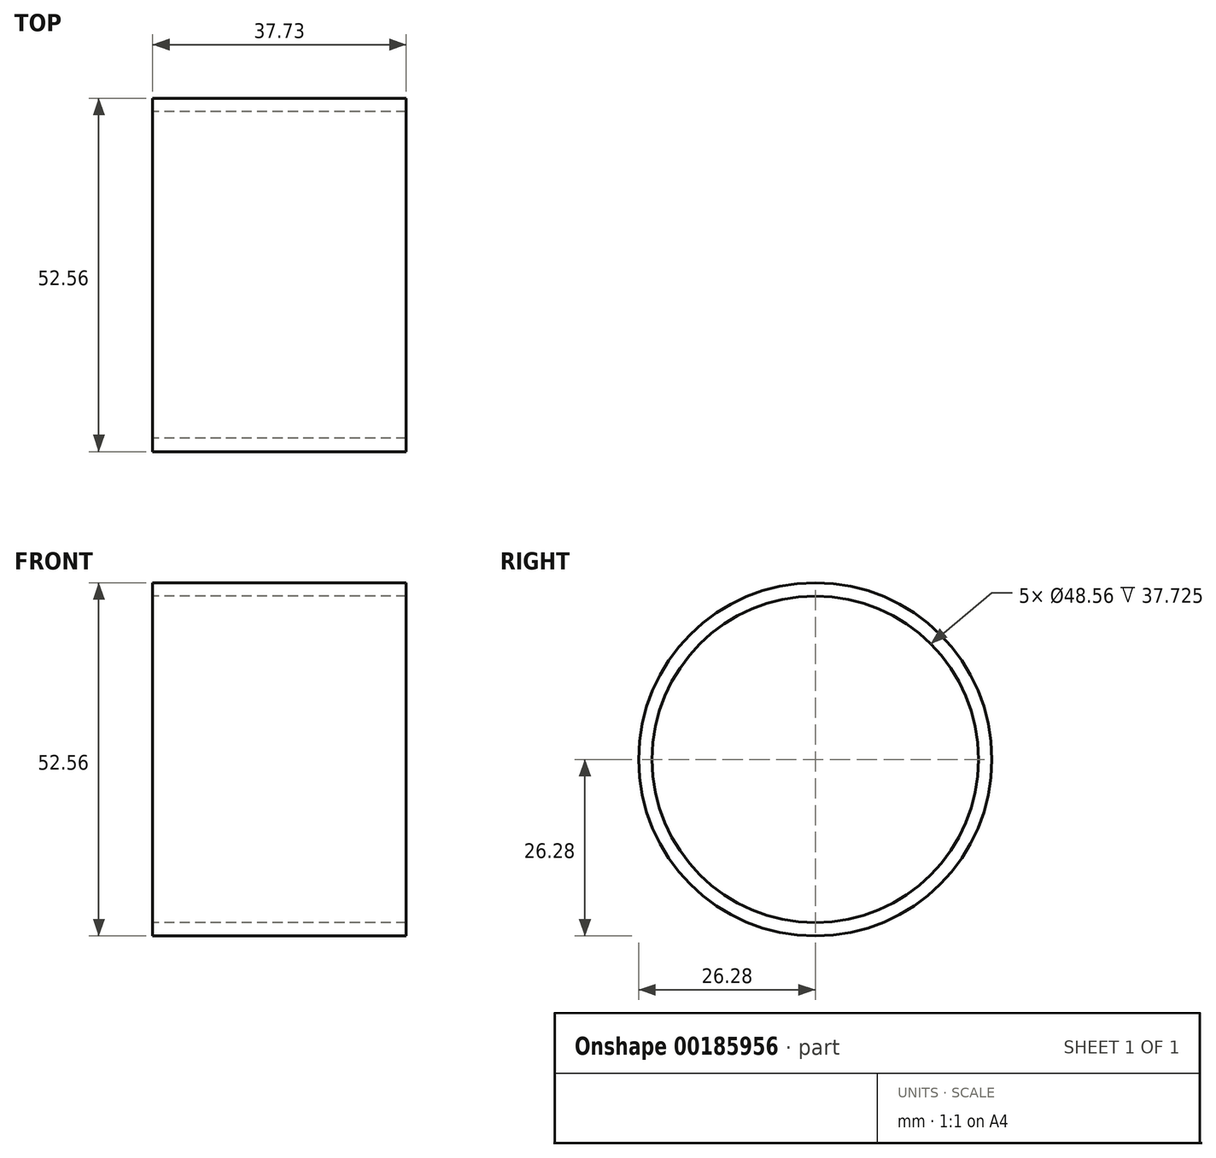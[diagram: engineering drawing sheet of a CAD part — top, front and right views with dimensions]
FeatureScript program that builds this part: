
annotation { "Feature Type Name" : "Feature", "Feature Type Description" : "" }
export const myFeature = defineFeature(function(context is Context, id is Id, definition is map)
    precondition{}
    {
        {
            var Q0;
            Q0=qCreatedBy(makeId("Front.planeOp"),FACE);
            var sketch = newSketch(context, id + "F0", { "sketchPlane" : qUnion([Q0])});
            skLineSegment(sketch, "E0", {"start": v(-4.52, 0) * mm, "end": v(5.17, 0) * mm});
            skLineSegment(sketch, "E1", {"start": v(-15.36, 26.28) * mm, "end": v(11, 26.28) * mm});
            skLineSegment(sketch, "E2", {"start": v(-15.36, 26.28) * mm, "end": v(-15.36, 24.28) * mm});
            skLineSegment(sketch, "E3", {"start": v(-15.36, 24.28) * mm, "end": v(20.05, 24.28) * mm});
            skLineSegment(sketch, "E4", {"start": v(11, 26.28) * mm, "end": v(22.37, 26.28) * mm});
            skLineSegment(sketch, "E5", {"start": v(20.05, 24.28) * mm, "end": v(22.37, 24.28) * mm});
            skLineSegment(sketch, "E6", {"start": v(22.37, 24.28) * mm, "end": v(22.37, 26.28) * mm});
            skSolve(sketch);
        }
        {
            var Q0;
            Q0=makeQuery(id+"F0.imprint","IMPRINT",FACE,{"disambiguationData":[TD([[makeQuery(id+"F0.imprint","IMPRINT",EDGE,{"derivedFrom":sQuery(id+"F0.wireOp",EDGE,"E1")}),-1.0]])]});
            var Q1;
            Q1=sQuery(id+"F0.wireOp",EDGE,"E0");
            revolve(context, id + "F1", {"entities" : qUnion([Q0]), "axis" : qUnion([Q1]), "revolveType" : RevolveType.FULL});
        }
    });
